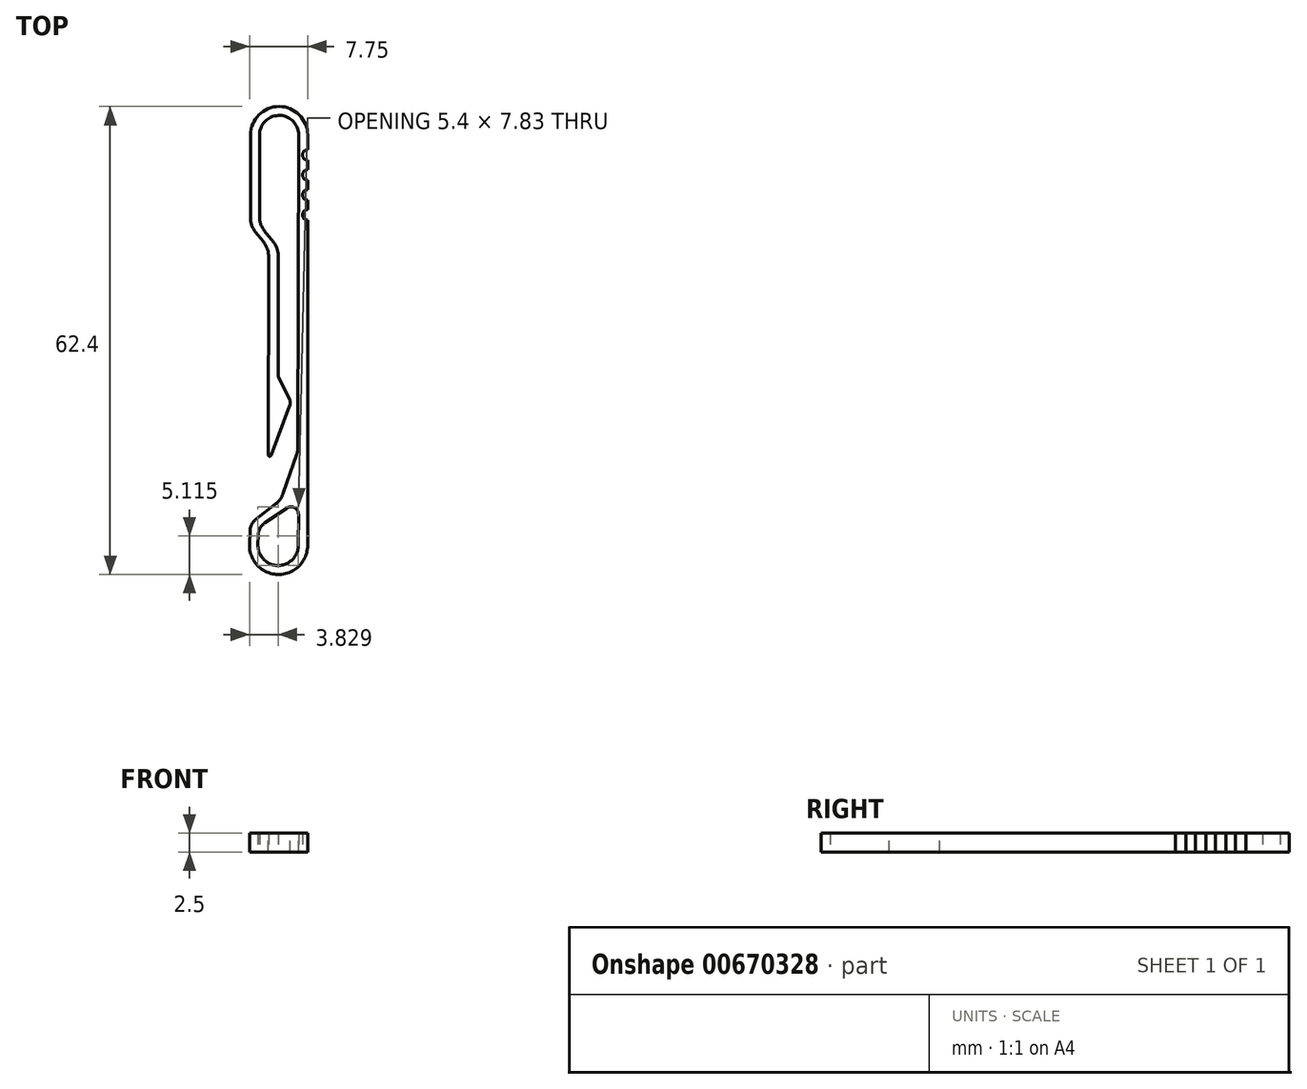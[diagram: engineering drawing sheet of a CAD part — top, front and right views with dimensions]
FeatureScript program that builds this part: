
annotation { "Feature Type Name" : "Feature", "Feature Type Description" : "" }
export const myFeature = defineFeature(function(context is Context, id is Id, definition is map)
    precondition{}
    {
        {
            var Q0;
            Q0=qCreatedBy(makeId("Top.planeOp"),FACE);
            var sketch = newSketch(context, id + "F0", { "sketchPlane" : qUnion([Q0])});
            skLineSegment(sketch, "E0", {"start": v(-3.84, -27.45) * mm, "end": v(-3.73, -24.72) * mm});
            skLineSegment(sketch, "E1", {"start": v(2.6, -14.97) * mm, "end": v(2.72, 27.11) * mm});
            skLineSegment(sketch, "E2", {"start": v(3.91, -27.6) * mm, "end": v(3.91, 16.46) * mm});
            skLineSegment(sketch, "E3", {"start": v(-2.71, -27.55) * mm, "end": v(-2.68, -25.24) * mm});
            skLineSegment(sketch, "E4", {"start": v(-2.68, -25.24) * mm, "end": v(2.7, -21.54) * mm});
            skLineSegment(sketch, "E5", {"start": v(2.7, -21.54) * mm, "end": v(2.67, -27.6) * mm});
            skArc(sketch, "E6", {"start": v(-2.71, -27.55) * mm, "mid": v(-0.05, -30.28) * mm, "end": v(2.67, -27.6) * mm});
            skArc(sketch, "E7", {"start": v(-3.84, -27.45) * mm, "mid": v(-0.04, -31.48) * mm, "end": v(3.91, -27.6) * mm});
            skLineSegment(sketch, "E8", {"start": v(-3.7, 27.11) * mm, "end": v(-3.71, 15) * mm});
            skLineSegment(sketch, "E9", {"start": v(1.7, -8.56) * mm, "end": v(-1.35, -16.62) * mm});
            skLineSegment(sketch, "E10", {"start": v(1.7, -8.56) * mm, "end": v(0, -5.14) * mm});
            skLineSegment(sketch, "E11", {"start": v(0, -5.14) * mm, "end": v(0, 12.04) * mm});
            skLineSegment(sketch, "E12", {"start": v(0, 12.04) * mm, "end": v(-2.5, 15.15) * mm});
            skLineSegment(sketch, "E13", {"start": v(-2.5, 15.15) * mm, "end": v(-2.5, 27.35) * mm});
            skArc(sketch, "E14", {"start": v(-3.7, 27.11) * mm, "mid": v(0.1, 30.92) * mm, "end": v(3.91, 27.11) * mm});
            skLineSegment(sketch, "E15", {"start": v(0.35, -21.56) * mm, "end": v(2.6, -14.97) * mm});
            skLineSegment(sketch, "E16", {"start": v(-1.3, 12.05) * mm, "end": v(-1.35, -16.62) * mm});
            skLineSegment(sketch, "E17", {"start": v(-1.3, 12.05) * mm, "end": v(-3.71, 15) * mm});
            skLineSegment(sketch, "E18", {"start": v(-3.73, -24.72) * mm, "end": v(0.35, -21.56) * mm});
            skArc(sketch, "E19", {"start": v(-2.5, 27.35) * mm, "mid": v(0.22, 29.73) * mm, "end": v(2.72, 27.11) * mm});
            skLineSegment(sketch, "E20", {"start": v(3.91, 16.46) * mm, "end": v(3.91, 19.13) * mm});
            skLineSegment(sketch, "E21", {"start": v(3.91, 21.79) * mm, "end": v(3.91, 24.45) * mm});
            skLineSegment(sketch, "E22", {"start": v(3.91, 24.45) * mm, "end": v(3.91, 27.11) * mm});
            skLineSegment(sketch, "E23", {"start": v(3.91, 19.13) * mm, "end": v(3.91, 21.79) * mm});
            skArc(sketch, "E24", {"start": v(3.91, 17.16) * mm, "mid": v(3.21, 16.46) * mm, "end": v(3.91, 15.76) * mm});
            skArc(sketch, "E25", {"start": v(3.91, 19.83) * mm, "mid": v(3.21, 19.13) * mm, "end": v(3.91, 18.43) * mm});
            skArc(sketch, "E26", {"start": v(3.91, 22.49) * mm, "mid": v(3.21, 21.79) * mm, "end": v(3.91, 21.09) * mm});
            skArc(sketch, "E27", {"start": v(3.91, 25.15) * mm, "mid": v(3.21, 24.45) * mm, "end": v(3.91, 23.75) * mm});
            skLineSegment(sketch, "E28", {"start": v(-2.71, -27.55) * mm, "end": v(2.67, -27.6) * mm});
            skSolve(sketch);
        }
        {
            var Q0;
            Q0=makeQuery(id+"F0.imprint","IMPRINT",FACE,{"disambiguationData":[TD([[makeQuery(id+"F0.imprint","IMPRINT",EDGE,{"derivedFrom":sQuery(id+"F0.wireOp",EDGE,"E0")}),-1.0]])]});
            extrude(context, id + "F1", {"entities" : qUnion([Q0]), "depth" : 2.5 * mm, "offsetDistance" : 25 * mm});
        }
        {
            var Q0;
            Q0=makeQuery(id+"F1.opExtrude","SWEPT_EDGE",EDGE,{"disambiguationData":[OSD([sQuery(id+"F0.wireOp",EDGE,"E4"),sQuery(id+"F0.wireOp",EDGE,"E5")])]});
            fillet(context, id + "F2", {"entities" : qUnion([Q0]), "radius" : 1 * mm, "tangentPropagation" : true, "allowEdgeOverflow" : false});
        }
        {
            var Q0;
            Q0=makeQuery(id+"F1.opExtrude","SWEPT_EDGE",EDGE,{"disambiguationData":[OSD([sQuery(id+"F0.wireOp",EDGE,"E9"),sQuery(id+"F0.wireOp",EDGE,"E16")])]});
            fillet(context, id + "F3", {"entities" : qUnion([Q0]), "radius" : 0.2 * mm, "tangentPropagation" : true, "allowEdgeOverflow" : false});
        }
        {
            var Q0;
            Q0=makeQuery(id+"F1.opExtrude","SWEPT_EDGE",EDGE,{"disambiguationData":[OSD([sQuery(id+"F0.wireOp",EDGE,"E9"),sQuery(id+"F0.wireOp",EDGE,"E10")])]});
            fillet(context, id + "F4", {"entities" : qUnion([Q0]), "radius" : 1 * mm, "tangentPropagation" : true, "allowEdgeOverflow" : false});
        }
        {
            var Q0;
            Q0=makeQuery(id+"F1.opExtrude","SWEPT_EDGE",EDGE,{"disambiguationData":[OSD([sQuery(id+"F0.wireOp",EDGE,"E12"),sQuery(id+"F0.wireOp",EDGE,"E13")])]});
            fillet(context, id + "F5", {"entities" : qUnion([Q0]), "radius" : 3 * mm, "tangentPropagation" : true, "allowEdgeOverflow" : false});
        }
        {
            var Q0;
            Q0=makeQuery(id+"F1.opExtrude","SWEPT_EDGE",EDGE,{"disambiguationData":[OSD([sQuery(id+"F0.wireOp",EDGE,"E8"),sQuery(id+"F0.wireOp",EDGE,"E17")])]});
            fillet(context, id + "F6", {"entities" : qUnion([Q0]), "radius" : 3 * mm, "tangentPropagation" : true, "allowEdgeOverflow" : false});
        }
        {
            var Q0;
            Q0=makeQuery(id+"F1.opExtrude","SWEPT_EDGE",EDGE,{"disambiguationData":[OSD([sQuery(id+"F0.wireOp",EDGE,"E16"),sQuery(id+"F0.wireOp",EDGE,"E17")])]});
            fillet(context, id + "F7", {"entities" : qUnion([Q0]), "radius" : 3 * mm, "tangentPropagation" : true, "allowEdgeOverflow" : false});
        }
        {
            var Q0;
            Q0=makeQuery(id+"F1.opExtrude","SWEPT_EDGE",EDGE,{"disambiguationData":[OSD([sQuery(id+"F0.wireOp",EDGE,"E11"),sQuery(id+"F0.wireOp",EDGE,"E12")])]});
            fillet(context, id + "F8", {"entities" : qUnion([Q0]), "radius" : 3 * mm, "tangentPropagation" : true, "allowEdgeOverflow" : false});
        }
        {
            var Q0;
            Q0=makeQuery(id+"F1.opExtrude","SWEPT_EDGE",EDGE,{"disambiguationData":[OSD([sQuery(id+"F0.wireOp",EDGE,"E0"),sQuery(id+"F0.wireOp",EDGE,"E18")])]});
            fillet(context, id + "F9", {"entities" : qUnion([Q0]), "radius" : 2 * mm, "tangentPropagation" : true, "allowEdgeOverflow" : false});
        }
        {
            var Q0;
            Q0=makeQuery(id+"F1.opExtrude","SWEPT_EDGE",EDGE,{"disambiguationData":[OSD([sQuery(id+"F0.wireOp",EDGE,"E3"),sQuery(id+"F0.wireOp",EDGE,"E4")])]});
            fillet(context, id + "F10", {"entities" : qUnion([Q0]), "radius" : 2 * mm, "tangentPropagation" : true, "allowEdgeOverflow" : false});
        }
        {
            var Q0;
            Q0=makeQuery(id+"F1.opExtrude","SWEPT_EDGE",EDGE,{"disambiguationData":[OSD([sQuery(id+"F0.wireOp",EDGE,"E15"),sQuery(id+"F0.wireOp",EDGE,"E18")])]});
            var Q1;
            Q1=makeQuery(id+"F1.opExtrude","SWEPT_EDGE",EDGE,{"disambiguationData":[OSD([sQuery(id+"F0.wireOp",EDGE,"E1"),sQuery(id+"F0.wireOp",EDGE,"E15")])]});
            fillet(context, id + "F11", {"entities" : qUnion([Q0, Q1]), "radius" : 3 * mm, "tangentPropagation" : true, "allowEdgeOverflow" : false});
        }
        {
            var Q0;
            Q0=makeQuery(id+"F1.opExtrude","SWEPT_EDGE",EDGE,{"disambiguationData":[OSD([sQuery(id+"F0.wireOp",EDGE,"E10"),sQuery(id+"F0.wireOp",EDGE,"E11")])]});
            fillet(context, id + "F12", {"entities" : qUnion([Q0]), "radius" : 1 * mm, "tangentPropagation" : true, "allowEdgeOverflow" : false});
        }
    });
